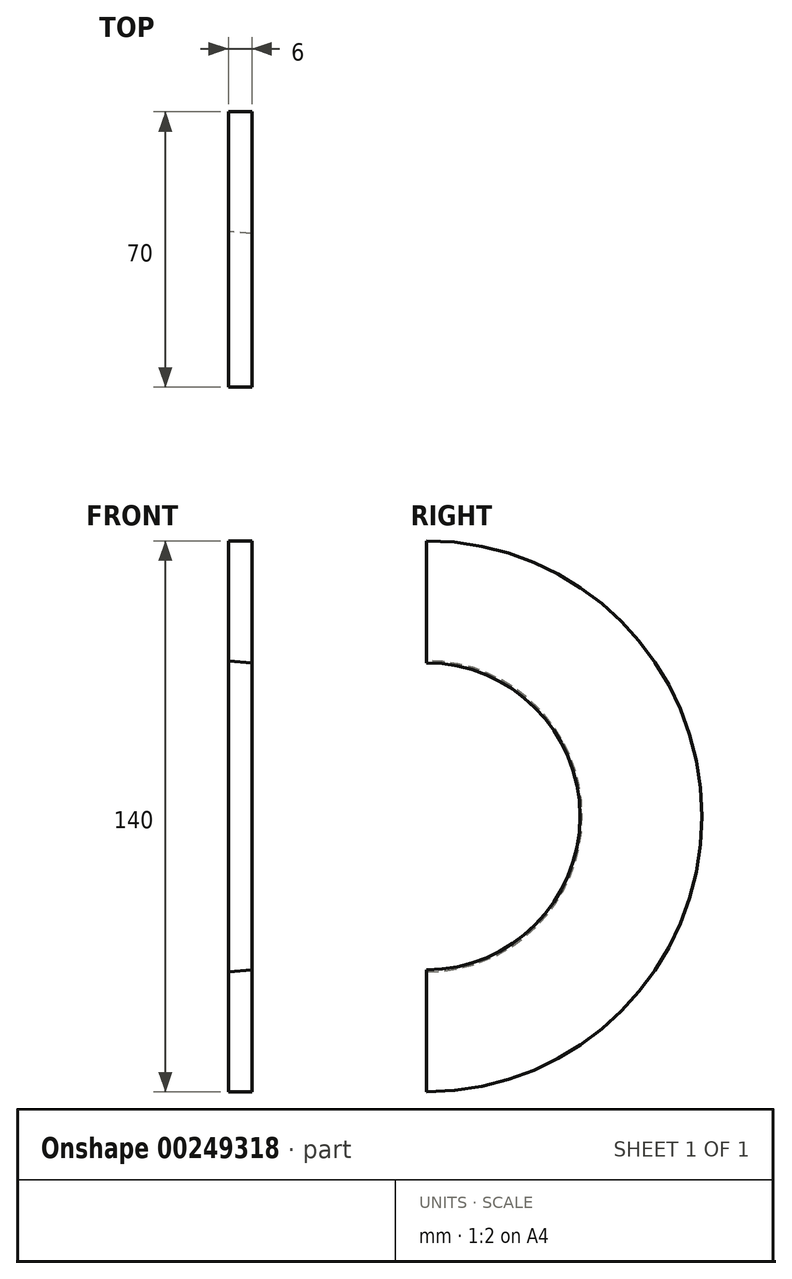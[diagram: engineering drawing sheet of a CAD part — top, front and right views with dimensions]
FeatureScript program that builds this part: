
annotation { "Feature Type Name" : "Feature", "Feature Type Description" : "" }
export const myFeature = defineFeature(function(context is Context, id is Id, definition is map)
    precondition{}
    {
        {
            var Q0;
            Q0=qCreatedBy(makeId("Front.planeOp"),FACE);
            var sketch = newSketch(context, id + "F0", { "sketchPlane" : qUnion([Q0])});
            skLineSegment(sketch, "E0", {"start": v(0, 39) * mm, "end": v(-6, 39.52) * mm});
            skLineSegment(sketch, "E1", {"start": v(-6, 39.52) * mm, "end": v(-6, 70) * mm});
            skLineSegment(sketch, "E2", {"start": v(-6, 70) * mm, "end": v(0, 70) * mm});
            skLineSegment(sketch, "E3", {"start": v(0, 70) * mm, "end": v(0, 39) * mm});
            skLineSegment(sketch, "E4", {"start": v(0, 0) * mm, "end": v(-46.92, 0) * mm});
            skSolve(sketch);
        }
        {
            var Q0;
            Q0=makeQuery(id+"F0.imprint","IMPRINT",FACE,{"disambiguationData":[TD([[makeQuery(id+"F0.imprint","IMPRINT",EDGE,{"derivedFrom":sQuery(id+"F0.wireOp",EDGE,"E0")}),-1.0]])]});
            var Q1;
            Q1=sQuery(id+"F0.wireOp",EDGE,"E4");
            revolve(context, id + "F1", {"entities" : qUnion([Q0]), "axis" : qUnion([Q1]), "revolveType" : RevolveType.ONE_DIRECTION, "angle" : 180 * degree});
        }
    });
